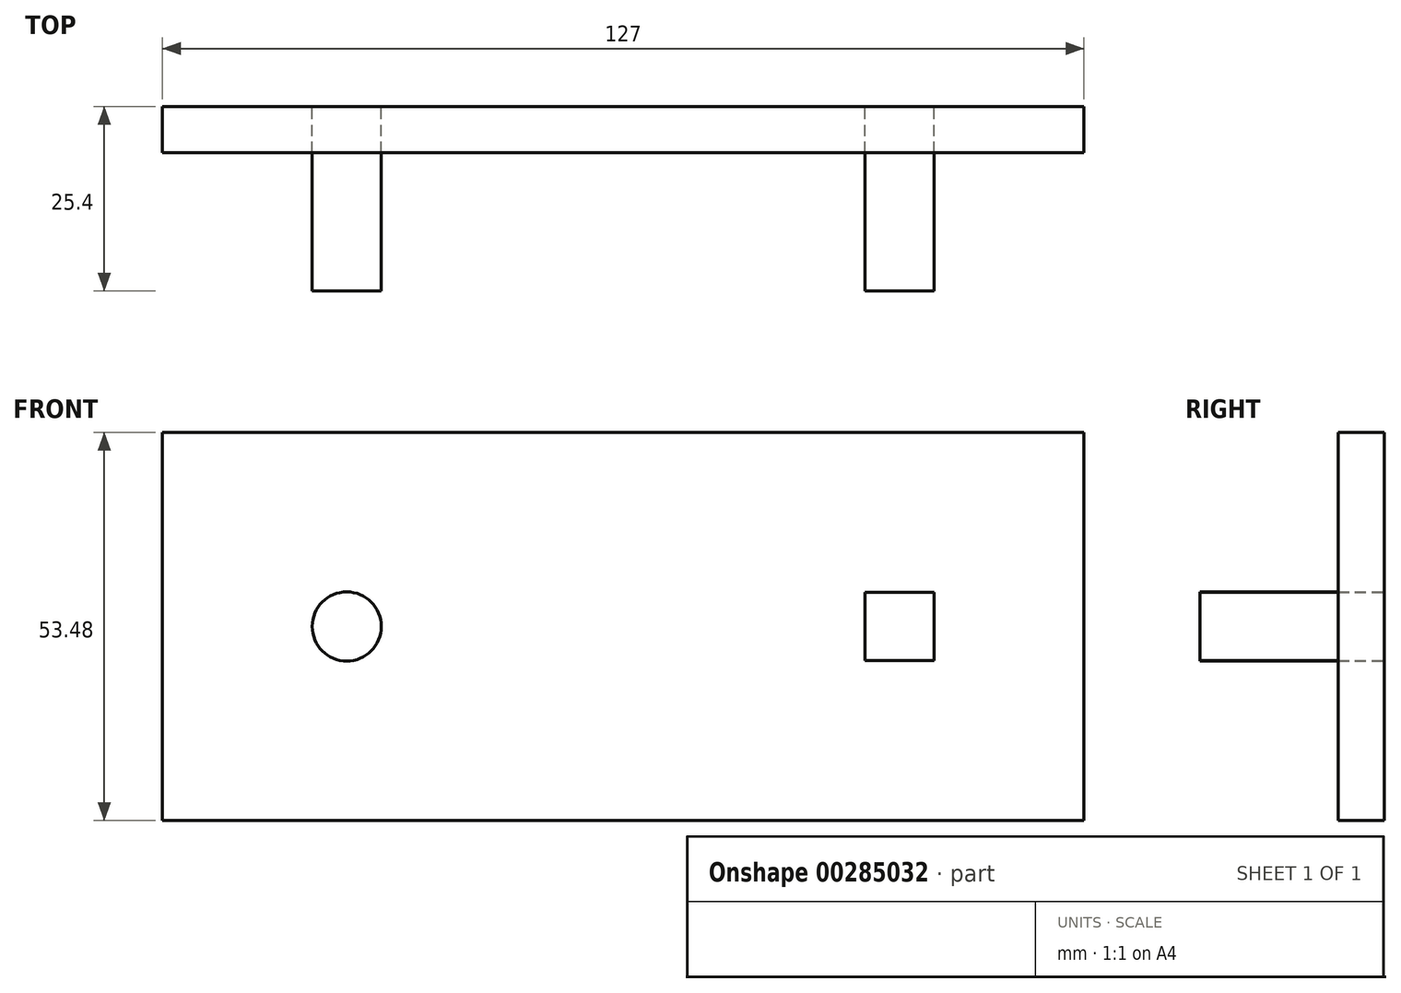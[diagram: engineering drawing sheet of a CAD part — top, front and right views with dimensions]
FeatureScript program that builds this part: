
annotation { "Feature Type Name" : "Feature", "Feature Type Description" : "" }
export const myFeature = defineFeature(function(context is Context, id is Id, definition is map)
    precondition{}
    {
        {
            var Q0;
            Q0=qCreatedBy(makeId("Front.planeOp"),FACE);
            var sketch = newSketch(context, id + "F0", { "sketchPlane" : qUnion([Q0])});
            skLineSegment(sketch, "E0.bottom", {"start": v(-89.31, 35.84) * mm, "end": v(37.69, 35.84) * mm});
            skLineSegment(sketch, "E0.top", {"start": v(-89.31, -17.64) * mm, "end": v(37.69, -17.64) * mm});
            skLineSegment(sketch, "E0.left", {"start": v(-89.31, 35.84) * mm, "end": v(-89.31, -17.64) * mm});
            skLineSegment(sketch, "E0.right", {"start": v(37.69, 35.84) * mm, "end": v(37.69, -17.64) * mm});
            skCircle(sketch, "E1", {"center": v(-63.91, 9.1) * mm, "radius": 4.76 * mm});
            skLineSegment(sketch, "E2.bottom", {"start": v(17.05, 13.8) * mm, "end": v(7.53, 13.8) * mm});
            skLineSegment(sketch, "E2.top", {"start": v(17.05, 4.4) * mm, "end": v(7.53, 4.4) * mm});
            skLineSegment(sketch, "E2.left", {"start": v(17.05, 13.8) * mm, "end": v(17.05, 4.4) * mm});
            skLineSegment(sketch, "E2.right", {"start": v(7.53, 13.8) * mm, "end": v(7.53, 4.4) * mm});
            skPoint(sketch, "E2.middle", {"position": v(12.29, 9.1) * mm});
            skSolve(sketch);
        }
        {
            var Q0;
            Q0=makeQuery(id+"F0.imprint","IMPRINT",FACE,{"disambiguationData":[TD([[makeQuery(id+"F0.imprint","IMPRINT",EDGE,{"derivedFrom":sQuery(id+"F0.wireOp",EDGE,"E0.bottom")}),-1.0]])]});
            var Q1;
            Q1=makeQuery(id+"F0.imprint","IMPRINT",FACE,{"disambiguationData":[TD([[makeQuery(id+"F0.imprint","IMPRINT",EDGE,{"derivedFrom":sQuery(id+"F0.wireOp",EDGE,"E1")}),1.0]])]});
            var Q2;
            Q2=makeQuery(id+"F0.imprint","IMPRINT",FACE,{"disambiguationData":[TD([[makeQuery(id+"F0.imprint","IMPRINT",EDGE,{"derivedFrom":sQuery(id+"F0.wireOp",EDGE,"E2.bottom")}),1.0]])]});
            extrude(context, id + "F1", {"entities" : qUnion([Q0, Q1, Q2]), "depth" : 6.35 * mm});
        }
        {
            var Q0;
            Q0=makeQuery(id+"F0.imprint","IMPRINT",FACE,{"disambiguationData":[TD([[makeQuery(id+"F0.imprint","IMPRINT",EDGE,{"derivedFrom":sQuery(id+"F0.wireOp",EDGE,"E1")}),1.0]])]});
            var Q1;
            Q1=makeQuery(id+"F0.imprint","IMPRINT",FACE,{"disambiguationData":[TD([[makeQuery(id+"F0.imprint","IMPRINT",EDGE,{"derivedFrom":sQuery(id+"F0.wireOp",EDGE,"E2.bottom")}),1.0]])]});
            extrude(context, id + "F2", {"entities" : qUnion([Q0, Q1]), "depth" : 25.4 * mm});
        }
    });
